# Revit family: LSTP 1x4
name_source: partatom
category: Lighting Fixtures
units: mm (PartAtom-declared; Revit-internal decimal feet)

## family parameters
Always vertical = Yes
Cut with Voids When Loaded = No
Host = Ceiling
Light Source = Yes
OmniClass Number = 23.80.70.11.14.17
OmniClass Title = Direct/Indirect
Part Type = Normal
Room Calculation Point = No
Round Connector Dimension = Use Diameter
Shared = No

## types (3) — shared parameters
Assembly Code = D5020200
Color Filter = 16777215
Description = LED Surface  Type P
Dimming Lamp Color Temperature Shift = <None>
Emit Shape Visible in Rendering = No
Emit from Rectangle Length = 3' - 11 3/4"
Emit from Rectangle Width = 0' - 11 3/4"
Housing Finish = Metal - Viscor - White
Lamp = LED
Length = 3' - 11 3/4"
Lens Finish = Polycarbonate - Viscor - Frosted Curved
Manufacturer = VISIONEERING by VISCOR
Model = LSTP
Reflector Width = 0' - 5 7/8"
Tilt Angle = 90.00°
URL = https://www.viscor.com
Voltage = 120 V
Width = 0' - 11 3/4"

## per-type parameters (varying)
| type | Apparent Load | Lamp Wattage | Photometric Web File |
| LSTP1x4-LED840K035LUNV | 29 VA | 29 VA | LSTP1X4-LED840K035LUNV.IES |
| LSTP1x4-LED840K040LUNV | 31 VA | 31 VA | LSTP1X4-LED840K040LUNV.IES |
| LSTP1x4-LED840K050LUNV | 39 VA | 39 VA | LSTP1X4-LED840K050LUNV.IES |

## geometry (parser evidence)
native form markers: Sweep x3
no freeform markers — native parametric forms only
